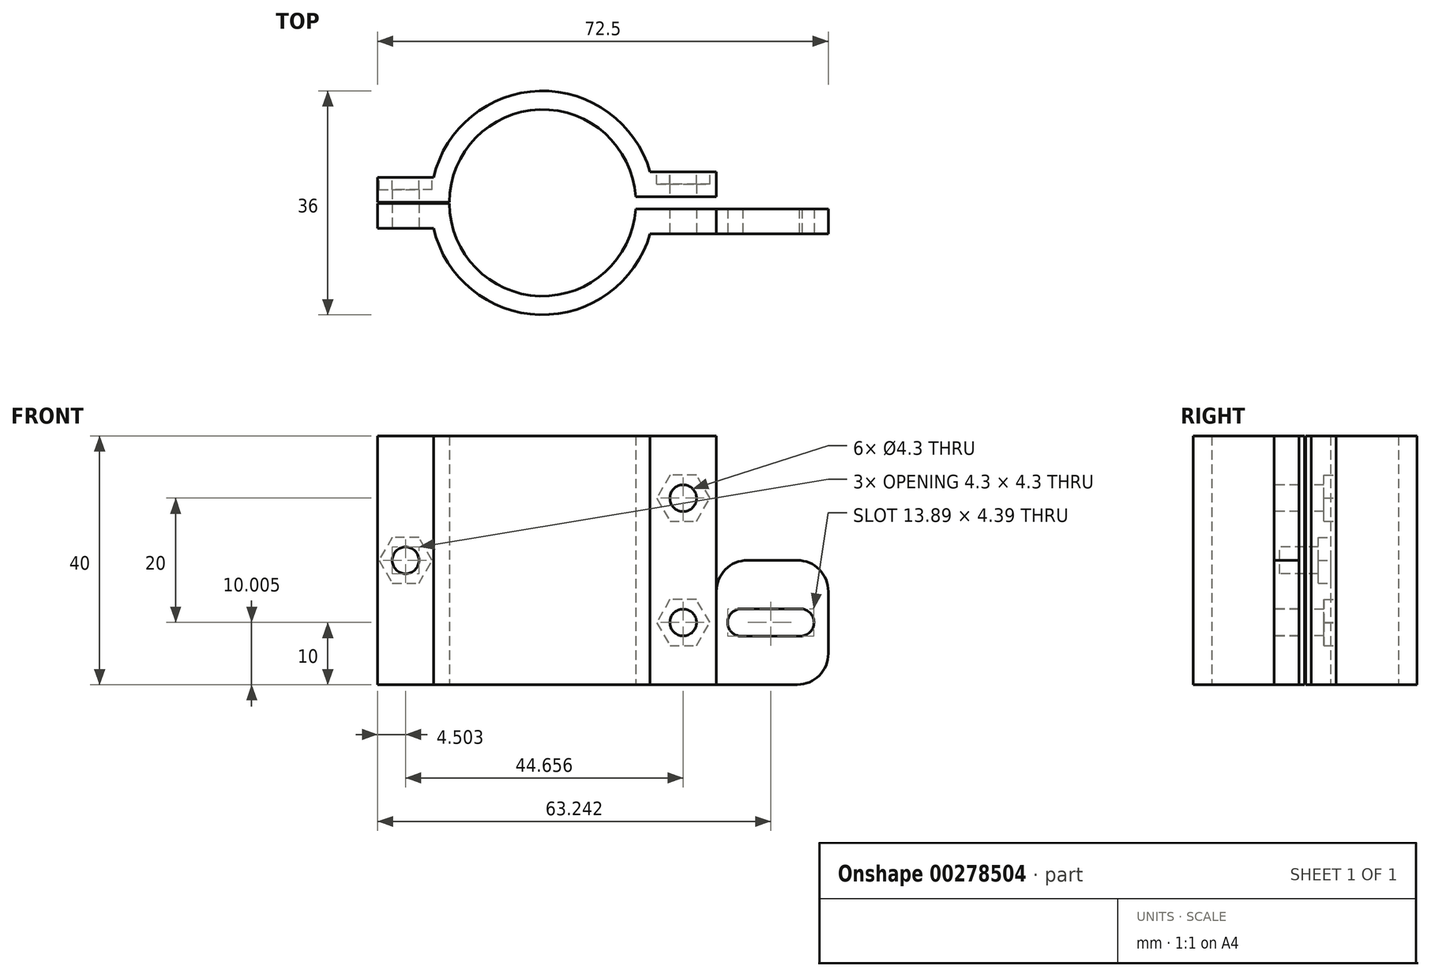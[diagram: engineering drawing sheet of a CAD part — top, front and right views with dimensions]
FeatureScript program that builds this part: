
annotation { "Feature Type Name" : "Feature", "Feature Type Description" : "" }
export const myFeature = defineFeature(function(context is Context, id is Id, definition is map)
    precondition{}
    {
        {
            var Q0;
            Q0=qCreatedBy(makeId("Top.planeOp"),FACE);
            var sketch = newSketch(context, id + "F0", { "sketchPlane" : qUnion([Q0])});
            skCircle(sketch, "E0", {"center": v(0, 0) * mm, "radius": 15 * mm});
            skCircle(sketch, "E1", {"center": v(0, 0) * mm, "radius": 18 * mm});
            skLineSegment(sketch, "E2", {"start": v(14.97, 1) * mm, "end": v(27.97, 1) * mm});
            skLineSegment(sketch, "E3", {"start": v(27.97, 1) * mm, "end": v(27.97, 5) * mm});
            skLineSegment(sketch, "E4", {"start": v(27.97, 5) * mm, "end": v(17.3, 5) * mm});
            skLineSegment(sketch, "E5.MirrorCS", {"start": v(14.97, -1) * mm, "end": v(27.97, -1) * mm});
            skLineSegment(sketch, "E6.MirrorCS", {"start": v(27.97, -5) * mm, "end": v(17.3, -5) * mm});
            skLineSegment(sketch, "E7.MirrorCS", {"start": v(27.97, -1) * mm, "end": v(27.97, -5) * mm});
            skLineSegment(sketch, "E8", {"start": v(-17.53, 4.1) * mm, "end": v(-26.53, 4.1) * mm});
            skLineSegment(sketch, "E9", {"start": v(-26.53, 4.1) * mm, "end": v(-26.53, 0.1) * mm});
            skLineSegment(sketch, "E10", {"start": v(-26.53, 0.1) * mm, "end": v(-15, 0.1) * mm});
            skLineSegment(sketch, "E11.MirrorCS", {"start": v(-26.53, -0.1) * mm, "end": v(-15, -0.1) * mm});
            skLineSegment(sketch, "E12.MirrorCS", {"start": v(-17.53, -4.1) * mm, "end": v(-26.53, -4.1) * mm});
            skLineSegment(sketch, "E13.MirrorCS", {"start": v(-26.53, -4.1) * mm, "end": v(-26.53, -0.1) * mm});
            skSolve(sketch);
        }
        {
            var Q0;
            {var subQ5=sQuery(id+"F0.wireOp",EDGE,"E2");var subQ7=sQuery(id+"F0.wireOp",EDGE,"E0");var subQ8=makeQuery(id+"F0.imprint","INTERSECT",VERTEX,{"derivedFrom":[subQ7,subQ5]});Q0=makeQuery(id+"F0.imprint","IMPRINT",FACE,{"disambiguationData":[TD([[makeQuery(id+"F0.imprint","IMPRINT",EDGE,{"disambiguationData":[TD([[subQ8,-1.0]])],"derivedFrom":subQ7}),-1.0]])]});}
            var Q1;
            {var subQ0=sQuery(id+"F0.wireOp",EDGE,"E8");Q1=makeQuery(id+"F0.imprint","IMPRINT",FACE,{"disambiguationData":[TD([[makeQuery(id+"F0.imprint","IMPRINT",EDGE,{"derivedFrom":subQ0}),1.0]])]});}
            var Q2;
            {var subQ0=sQuery(id+"F0.wireOp",EDGE,"E12.MirrorCS");Q2=makeQuery(id+"F0.imprint","IMPRINT",FACE,{"disambiguationData":[TD([[makeQuery(id+"F0.imprint","IMPRINT",EDGE,{"derivedFrom":subQ0}),-1.0]])]});}
            var Q3;
            {var subQ2=sQuery(id+"F0.wireOp",EDGE,"E5.MirrorCS");var subQ7=sQuery(id+"F0.wireOp",EDGE,"E0");var subQ8=makeQuery(id+"F0.imprint","INTERSECT",VERTEX,{"derivedFrom":[subQ7,subQ2]});Q3=makeQuery(id+"F0.imprint","IMPRINT",FACE,{"disambiguationData":[TD([[makeQuery(id+"F0.imprint","IMPRINT",EDGE,{"disambiguationData":[TD([[subQ8,1.0]])],"derivedFrom":subQ7}),-1.0]])]});}
            var Q4;
            {var subQ0=sQuery(id+"F0.wireOp",EDGE,"E6.MirrorCS");Q4=makeQuery(id+"F0.imprint","IMPRINT",FACE,{"disambiguationData":[TD([[makeQuery(id+"F0.imprint","IMPRINT",EDGE,{"derivedFrom":subQ0}),-1.0]])]});}
            var Q5;
            {var subQ4=sQuery(id+"F0.wireOp",EDGE,"E3");Q5=makeQuery(id+"F0.imprint","IMPRINT",FACE,{"disambiguationData":[TD([[makeQuery(id+"F0.imprint","IMPRINT",EDGE,{"derivedFrom":subQ4}),1.0]])]});}
            extrude(context, id + "F1", {"entities" : qUnion([Q0, Q1, Q2, Q3, Q4, Q5]), "depth" : 40 * mm, "symmetric" : true});
        }
        {
            var Q0;
            Q0=makeQuery(id+"F1.opExtrude","SWEPT_FACE",FACE,{"disambiguationData":[OSD([sQuery(id+"F0.wireOp",EDGE,"E12.MirrorCS")])]});
            var sketch = newSketch(context, id + "F2", { "sketchPlane" : qUnion([Q0])});
            skCircle(sketch, "E14", {"center": v(-22.03, 0) * mm, "radius": 2.15 * mm});
            skSolve(sketch);
        }
        {
            var Q0;
            Q0=makeQuery(id+"F2.imprint","IMPRINT",FACE,{"disambiguationData":[TD([[makeQuery(id+"F2.imprint","IMPRINT",EDGE,{"derivedFrom":sQuery(id+"F2.wireOp",EDGE,"E14")}),1.0]])]});
            extrude(context, id + "F3", {"entities" : qUnion([Q0]), "operationType" : NewBodyOperationType.REMOVE, "oppositeDirection" : true, "depth" : 25 * mm});
        }
        {
            var Q0;
            Q0=makeQuery(id+"F1.opExtrude","SWEPT_FACE",FACE,{"disambiguationData":[OSD([sQuery(id+"F0.wireOp",EDGE,"E8")])]});
            var sketch = newSketch(context, id + "F4", { "sketchPlane" : qUnion([Q0])});
            skCircle(sketch, "E15.cCircle", {"center": v(22.03, 0) * mm, "radius": 3.7 * mm, "construction": true});
            skLineSegment(sketch, "E15.0", {"start": v(19.9, 3.7) * mm, "end": v(24.16, 3.7) * mm});
            skLineSegment(sketch, "E15.1", {"start": v(24.16, 3.7) * mm, "end": v(26.3, 0) * mm});
            skLineSegment(sketch, "E15.2", {"start": v(26.3, 0) * mm, "end": v(24.16, -3.7) * mm});
            skLineSegment(sketch, "E15.3", {"start": v(24.16, -3.7) * mm, "end": v(19.9, -3.7) * mm});
            skLineSegment(sketch, "E15.4", {"start": v(19.9, -3.7) * mm, "end": v(17.75, 0) * mm});
            skLineSegment(sketch, "E15.5", {"start": v(17.75, 0) * mm, "end": v(19.9, 3.7) * mm});
            skPoint(sketch, "E15.0.midPoint", {"position": v(22.03, 3.7) * mm});
            skSolve(sketch);
        }
        {
            var Q0;
            {var subQ6=sQuery(id+"F4.wireOp",EDGE,"E15.0");Q0=makeQuery(id+"F4.imprint","IMPRINT",FACE,{"disambiguationData":[TD([[makeQuery(id+"F4.imprint","IMPRINT",EDGE,{"derivedFrom":subQ6}),-1.0]])]});}
            extrude(context, id + "F5", {"entities" : qUnion([Q0]), "operationType" : NewBodyOperationType.REMOVE, "oppositeDirection" : true, "depth" : 2 * mm});
        }
        {
            var Q0;
            Q0=makeQuery(id+"F1.opExtrude","SWEPT_FACE",FACE,{"disambiguationData":[OSD([sQuery(id+"F0.wireOp",EDGE,"E6.MirrorCS")])]});
            var sketch = newSketch(context, id + "F6", { "sketchPlane" : qUnion([Q0])});
            skCircle(sketch, "E16", {"center": v(22.63, 10) * mm, "radius": 2.15 * mm});
            skCircle(sketch, "E17", {"center": v(22.63, -10) * mm, "radius": 2.15 * mm});
            skLineSegment(sketch, "E18", {"start": v(22.63, 20) * mm, "end": v(22.63, -20) * mm, "construction": true});
            skSolve(sketch);
        }
        {
            var Q0;
            Q0=makeQuery(id+"F6.imprint","IMPRINT",FACE,{"disambiguationData":[TD([[makeQuery(id+"F6.imprint","IMPRINT",EDGE,{"derivedFrom":sQuery(id+"F6.wireOp",EDGE,"E16")}),1.0]])]});
            var Q1;
            Q1=makeQuery(id+"F6.imprint","IMPRINT",FACE,{"disambiguationData":[TD([[makeQuery(id+"F6.imprint","IMPRINT",EDGE,{"derivedFrom":sQuery(id+"F6.wireOp",EDGE,"E17")}),1.0]])]});
            extrude(context, id + "F7", {"entities" : qUnion([Q0, Q1]), "operationType" : NewBodyOperationType.REMOVE, "oppositeDirection" : true, "depth" : 25 * mm});
        }
        {
            var Q0;
            Q0=makeQuery(id+"F1.opExtrude","SWEPT_FACE",FACE,{"disambiguationData":[OSD([sQuery(id+"F0.wireOp",EDGE,"E4")])]});
            var sketch = newSketch(context, id + "F8", { "sketchPlane" : qUnion([Q0])});
            skCircle(sketch, "E19.cCircle", {"center": v(-22.63, 10) * mm, "radius": 3.7 * mm, "construction": true});
            skLineSegment(sketch, "E19.0", {"start": v(-24.77, 13.7) * mm, "end": v(-20.5, 13.7) * mm});
            skLineSegment(sketch, "E19.1", {"start": v(-20.5, 13.7) * mm, "end": v(-18.36, 10) * mm});
            skLineSegment(sketch, "E19.2", {"start": v(-18.36, 10) * mm, "end": v(-20.5, 6.3) * mm});
            skLineSegment(sketch, "E19.3", {"start": v(-20.5, 6.3) * mm, "end": v(-24.77, 6.3) * mm});
            skLineSegment(sketch, "E19.4", {"start": v(-24.77, 6.3) * mm, "end": v(-26.9, 10) * mm});
            skLineSegment(sketch, "E19.5", {"start": v(-26.9, 10) * mm, "end": v(-24.77, 13.7) * mm});
            skPoint(sketch, "E19.0.midPoint", {"position": v(-22.63, 13.7) * mm});
            skCircle(sketch, "E20.cCircle", {"center": v(-22.63, -10) * mm, "radius": 3.7 * mm, "construction": true});
            skLineSegment(sketch, "E20.0", {"start": v(-24.76, -6.3) * mm, "end": v(-20.49, -6.3) * mm});
            skLineSegment(sketch, "E20.1", {"start": v(-20.49, -6.3) * mm, "end": v(-18.36, -10) * mm});
            skLineSegment(sketch, "E20.2", {"start": v(-18.36, -10) * mm, "end": v(-20.5, -13.7) * mm});
            skLineSegment(sketch, "E20.3", {"start": v(-20.5, -13.7) * mm, "end": v(-24.77, -13.7) * mm});
            skLineSegment(sketch, "E20.4", {"start": v(-24.77, -13.7) * mm, "end": v(-26.9, -10) * mm});
            skLineSegment(sketch, "E20.5", {"start": v(-26.9, -10) * mm, "end": v(-24.76, -6.3) * mm});
            skPoint(sketch, "E20.0.midPoint", {"position": v(-22.62, -6.3) * mm});
            skSolve(sketch);
        }
        {
            var Q0;
            Q0=makeQuery(id+"F8.imprint","IMPRINT",FACE,{"disambiguationData":[TD([[makeQuery(id+"F8.imprint","IMPRINT",EDGE,{"derivedFrom":sQuery(id+"F8.wireOp",EDGE,"E19.0")}),-1.0]])]});
            var Q1;
            Q1=makeQuery(id+"F8.imprint","IMPRINT",FACE,{"disambiguationData":[TD([[makeQuery(id+"F8.imprint","IMPRINT",EDGE,{"derivedFrom":sQuery(id+"F8.wireOp",EDGE,"E20.0")}),-1.0]])]});
            extrude(context, id + "F9", {"entities" : qUnion([Q0, Q1]), "operationType" : NewBodyOperationType.REMOVE, "oppositeDirection" : true, "depth" : 2 * mm});
        }
        {
            var Q0;
            Q0=makeQuery(id+"F1.opExtrude","SWEPT_FACE",FACE,{"disambiguationData":[OSD([sQuery(id+"F0.wireOp",EDGE,"E7.MirrorCS")])]});
            var sketch = newSketch(context, id + "F10", { "sketchPlane" : qUnion([Q0])});
            skLineSegment(sketch, "E21.bottom", {"start": v(-5, 0) * mm, "end": v(-1, 0) * mm});
            skLineSegment(sketch, "E21.top", {"start": v(-5, 20) * mm, "end": v(-1, 20) * mm});
            skLineSegment(sketch, "E21.left", {"start": v(-5, 0) * mm, "end": v(-5, 20) * mm});
            skLineSegment(sketch, "E21.right", {"start": v(-1, 0) * mm, "end": v(-1, 20) * mm});
            skSolve(sketch);
        }
        {
            var Q0;
            Q0=makeQuery(id+"F10.imprint","IMPRINT",FACE,{"disambiguationData":[TD([[makeQuery(id+"F10.imprint","IMPRINT",EDGE,{"derivedFrom":sQuery(id+"F10.wireOp",EDGE,"E21.bottom")}),1.0]])]});
            extrude(context, id + "F11", {"entities" : qUnion([Q0]), "depth" : 18 * mm});
        }
        {
            var Q0;
            Q0=makeQuery(id+"F11.opExtrude","CAP_EDGE",EDGE,{"disambiguationData":[OSD([sQuery(id+"F10.wireOp",EDGE,"E21.top")])],"isStart":false});
            var Q1;
            Q1=makeQuery(id+"F11.opExtrude","CAP_EDGE",EDGE,{"disambiguationData":[OSD([sQuery(id+"F10.wireOp",EDGE,"E21.bottom")])],"isStart":false});
            fillet(context, id + "F12", {"entities" : qUnion([Q0, Q1]), "radius" : 5 * mm, "tangentPropagation" : true, "allowEdgeOverflow" : false});
        }
        {
            var Q0;
            Q0=makeQuery(id+"F11.opExtrude","SWEPT_FACE",FACE,{"disambiguationData":[OSD([sQuery(id+"F10.wireOp",EDGE,"E21.left")])]});
            var sketch = newSketch(context, id + "F13", { "sketchPlane" : qUnion([Q0])});
            skCircle(sketch, "E22", {"center": v(31.97, 10) * mm, "radius": 2.2 * mm});
            skPoint(sketch, "E22.centerSnap0", {"position": v(27.97, 10) * mm});
            skCircle(sketch, "E23", {"center": v(41.47, 10) * mm, "radius": 2.2 * mm});
            skLineSegment(sketch, "E24", {"start": v(32.17, 12.2) * mm, "end": v(41.26, 12.2) * mm});
            skLineSegment(sketch, "E25", {"start": v(41.7, 7.81) * mm, "end": v(31.97, 7.8) * mm});
            skSolve(sketch);
        }
        {
            var Q0;
            {var subQ0=sQuery(id+"F13.wireOp",EDGE,"E22");var subQ1=makeQuery(id+"F13.imprint","INTERSECT",VERTEX,{"derivedFrom":[subQ0,sQuery(id+"F13.wireOp",EDGE,"E24")]});Q0=makeQuery(id+"F13.imprint","IMPRINT",FACE,{"disambiguationData":[TD([[makeQuery(id+"F13.imprint","IMPRINT",EDGE,{"disambiguationData":[TD([[subQ1,-1.0]])],"derivedFrom":subQ0}),1.0]])]});}
            var Q1;
            {var subQ0=sQuery(id+"F13.wireOp",EDGE,"E23");var subQ1=makeQuery(id+"F13.imprint","INTERSECT",VERTEX,{"derivedFrom":[subQ0,sQuery(id+"F13.wireOp",EDGE,"E24")]});Q1=makeQuery(id+"F13.imprint","IMPRINT",FACE,{"disambiguationData":[TD([[makeQuery(id+"F13.imprint","IMPRINT",EDGE,{"disambiguationData":[TD([[subQ1,-1.0]])],"derivedFrom":subQ0}),1.0]])]});}
            var Q2;
            {var subQ0=sQuery(id+"F13.wireOp",EDGE,"E24");Q2=makeQuery(id+"F13.imprint","IMPRINT",FACE,{"disambiguationData":[TD([[makeQuery(id+"F13.imprint","IMPRINT",EDGE,{"derivedFrom":subQ0}),-1.0]])]});}
            extrude(context, id + "F14", {"entities" : qUnion([Q0, Q1, Q2]), "operationType" : NewBodyOperationType.REMOVE, "oppositeDirection" : true, "depth" : 25 * mm});
        }
        {
            var Q0;
            Q0=makeQuery(id+"F11.opExtrude","SWEPT_BODY",BODY,{"disambiguationData":[OSD([sQuery(id+"F10.wireOp",EDGE,"E21.bottom"),sQuery(id+"F10.wireOp",EDGE,"E21.top"),sQuery(id+"F10.wireOp",EDGE,"E21.left"),sQuery(id+"F10.wireOp",EDGE,"E21.right")])]});
            var Q1;
            Q1=qCreatedBy(makeId("Top.planeOp"),FACE);
            mirror(context, id + "F15", {"entities" : qUnion([Q0]), "mirrorPlane" : qUnion([Q1])});
        }
        {
            var Q0;
            Q0=makeQuery(id+"F11.opExtrude","SWEPT_BODY",BODY,{"disambiguationData":[OSD([sQuery(id+"F10.wireOp",EDGE,"E21.bottom"),sQuery(id+"F10.wireOp",EDGE,"E21.top"),sQuery(id+"F10.wireOp",EDGE,"E21.left"),sQuery(id+"F10.wireOp",EDGE,"E21.right")])]});
            deleteBodies(context, id + "F16", {"entities" : qUnion([Q0])});
        }
        {
            var Q0;
            Q0=makeQuery(id+"F15.opPattern","COPY",EDGE,{"derivedFrom":makeQuery(id+"F11.opExtrude","CAP_EDGE",EDGE,{"disambiguationData":[OSD([sQuery(id+"F10.wireOp",EDGE,"E21.bottom")])],"isStart":true}),"instanceName":"1"});
            fillet(context, id + "F17", {"entities" : qUnion([Q0]), "radius" : 5 * mm, "tangentPropagation" : true, "allowEdgeOverflow" : false});
        }
    });
